FCSTD DOCUMENT  (FreeCAD 0.18R16146 (Git))
Label: mk-ltk-01_case-cover
License: All rights reserved
LicenseURL: http://en.wikipedia.org/wiki/All_rights_reserved
objects: Sketcher::SketchObject×12
note: 12 computed .brp shape members not serialized (recipe doc carries the construction recipe); baked Part::Feature solids carry a one-line shape summary decoded from their .brp

FEATURE [Sketcher::SketchObject] Sketch084  label="outer edge"
  MapMode = 2
  sketch-geometry (84):
    g0: LineSegment StartX=2.096 StartY=136.077 StartZ=0 EndX=419.671 EndY=136.077 EndZ=0
    g1: LineSegment StartX=421.665 StartY=134.233 StartZ=0 EndX=421.672 EndY=134.076 EndZ=0
    g2: LineSegment StartX=421.291 StartY=135.253 StartZ=0 EndX=421.375 EndY=135.122 EndZ=0
    g3: LineSegment StartX=421.647 StartY=134.39 StartZ=0 EndX=421.665 EndY=134.233 EndZ=0
    g4: LineSegment StartX=421.573 StartY=134.696 StartZ=0 EndX=421.615 EndY=134.543 EndZ=0
    g5: LineSegment StartX=420.846 StartY=0.63252 StartZ=0 EndX=420.716 EndY=0.545705 EndZ=0
    g6: LineSegment StartX=420.716 StartY=0.545705 StartZ=0 EndX=420.578 EndY=0.468535 EndZ=0
    g7: LineSegment StartX=420.578 StartY=0.468535 StartZ=0 EndX=420.437 EndY=0.403765 EndZ=0
    g8: LineSegment StartX=420.437 StartY=0.403765 StartZ=0 EndX=420.289 EndY=0.348644 EndZ=0
    g9: LineSegment StartX=420.97 StartY=135.598 StartZ=0 EndX=421.086 EndY=135.491 EndZ=0
    g10: LineSegment StartX=419.671 StartY=136.077 StartZ=0 EndX=419.827 EndY=136.07 EndZ=0
    g11: LineSegment StartX=421.192 StartY=135.376 StartZ=0 EndX=421.291 EndY=135.253 EndZ=0
    g12: LineSegment StartX=421.453 StartY=134.984 StartZ=0 EndX=421.52 EndY=134.842 EndZ=0
    g13: LineSegment StartX=421.453 StartY=1.34359 StartZ=0 EndX=421.375 EndY=1.20716 EndZ=0
    g14: LineSegment StartX=421.647 StartY=1.9389 StartZ=0 EndX=421.615 EndY=1.78456 EndZ=0
    g15: LineSegment StartX=421.615 StartY=1.78456 StartZ=0 EndX=421.573 EndY=1.63298 EndZ=0
    g16: LineSegment StartX=421.086 StartY=0.836468 StartZ=0 EndX=420.97 EndY=0.730359 EndZ=0
    g17: LineSegment StartX=420.97 StartY=0.730359 StartZ=0 EndX=420.846 EndY=0.63252 EndZ=0
    g18: LineSegment StartX=421.615 StartY=134.543 StartZ=0 EndX=421.647 EndY=134.39 EndZ=0
    g19: LineSegment StartX=421.573 StartY=1.63298 StartZ=0 EndX=421.52 EndY=1.48553 EndZ=0
    g20: LineSegment StartX=421.52 StartY=1.48553 StartZ=0 EndX=421.453 EndY=1.34359 EndZ=0
    g21: LineSegment StartX=421.672 StartY=2.25034 StartZ=0 EndX=421.665 EndY=2.09462 EndZ=0
    g22: LineSegment StartX=1.18787 StartY=0.468535 StartZ=0 EndX=1.05006 EndY=0.545705 EndZ=0
    g23: LineSegment StartX=1.05006 StartY=0.545705 StartZ=0 EndX=0.919152 EndY=0.63252 EndZ=0
    g24: LineSegment StartX=0.919152 StartY=0.63252 StartZ=0 EndX=0.796505 EndY=0.730359 EndZ=0
    g25: LineSegment StartX=0.796505 StartY=0.730359 StartZ=0 EndX=0.680752 EndY=0.836468 EndZ=0
    g26: LineSegment StartX=421.52 StartY=134.842 StartZ=0 EndX=421.573 EndY=134.696 EndZ=0
    g27: LineSegment StartX=0.101975 StartY=134.233 StartZ=0 EndX=0.119889 EndY=134.39 EndZ=0
    g28: LineSegment StartX=0.119889 StartY=134.39 StartZ=0 EndX=0.150206 EndY=134.543 EndZ=0
    g29: LineSegment StartX=0.150206 StartY=134.543 StartZ=0 EndX=0.192925 EndY=134.696 EndZ=0
    g30: LineSegment StartX=0.192925 StartY=134.696 StartZ=0 EndX=0.248047 EndY=134.842 EndZ=0
    g31: LineSegment StartX=421.665 StartY=2.09462 StartZ=0 EndX=421.647 EndY=1.9389 EndZ=0
    g32: LineSegment StartX=0.680752 StartY=0.836468 StartZ=0 EndX=0.574643 EndY=0.952225 EndZ=0
    g33: LineSegment StartX=0.574643 StartY=0.952225 StartZ=0 EndX=0.4768 EndY=1.07625 EndZ=0
    g34: LineSegment StartX=0.4768 StartY=1.07625 StartZ=0 EndX=0.389985 EndY=1.20716 EndZ=0
    g35: LineSegment StartX=0.389985 StartY=1.20716 StartZ=0 EndX=0.312815 EndY=1.34359 EndZ=0
    g36: LineSegment StartX=0.312815 StartY=1.34359 StartZ=0 EndX=0.248047 EndY=1.48553 EndZ=0
    g37: LineSegment StartX=0.248047 StartY=1.48553 StartZ=0 EndX=0.192925 EndY=1.63298 EndZ=0
    g38: LineSegment StartX=0.192925 StartY=1.63298 StartZ=0 EndX=0.150206 EndY=1.78456 EndZ=0
    g39: LineSegment StartX=0.150206 StartY=1.78456 StartZ=0 EndX=0.119889 EndY=1.9389 EndZ=0
    g40: LineSegment StartX=420.289 StartY=135.979 StartZ=0 EndX=420.437 EndY=135.924 EndZ=0
    g41: LineSegment StartX=1.7818 StartY=0.275608 StartZ=0 EndX=1.62884 EndY=0.307303 EndZ=0
    g42: LineSegment StartX=1.62884 StartY=0.307303 StartZ=0 EndX=1.47588 EndY=0.348644 EndZ=0
    g43: LineSegment StartX=1.47588 StartY=0.348644 StartZ=0 EndX=1.32981 EndY=0.403765 EndZ=0
    g44: LineSegment StartX=1.32981 StartY=0.403765 StartZ=0 EndX=1.18787 EndY=0.468535 EndZ=0
    g45: LineSegment StartX=420.437 StartY=135.924 StartZ=0 EndX=420.578 EndY=135.859 EndZ=0
    g46: LineSegment StartX=419.982 StartY=136.052 StartZ=0 EndX=420.137 EndY=136.022 EndZ=0
    g47: LineSegment StartX=419.827 StartY=136.07 StartZ=0 EndX=419.982 EndY=136.052 EndZ=0
    g48: LineSegment StartX=420.846 StartY=135.695 StartZ=0 EndX=420.97 EndY=135.598 EndZ=0
    g49: LineSegment StartX=420.578 StartY=135.859 StartZ=0 EndX=420.716 EndY=135.782 EndZ=0
    g50: LineSegment StartX=419.827 StartY=0.257693 StartZ=0 EndX=419.671 EndY=0.250803 EndZ=0
    g51: LineSegment StartX=419.671 StartY=0.250803 StartZ=0 EndX=2.096 EndY=0.250803 EndZ=0
    g52: LineSegment StartX=2.096 StartY=0.250803 StartZ=0 EndX=1.9389 EndY=0.257693 EndZ=0
    g53: LineSegment StartX=1.9389 StartY=0.257693 StartZ=0 EndX=1.7818 EndY=0.275608 EndZ=0
    g54: LineSegment StartX=0.248047 StartY=134.842 StartZ=0 EndX=0.312815 EndY=134.984 EndZ=0
    g55: LineSegment StartX=0.312815 StartY=134.984 StartZ=0 EndX=0.389985 EndY=135.122 EndZ=0
    g56: LineSegment StartX=0.389985 StartY=135.122 StartZ=0 EndX=0.4768 EndY=135.253 EndZ=0
    g57: LineSegment StartX=0.4768 StartY=135.253 StartZ=0 EndX=0.574643 EndY=135.376 EndZ=0
    g58: LineSegment StartX=0.574643 StartY=135.376 StartZ=0 EndX=0.680752 EndY=135.491 EndZ=0
    g59: LineSegment StartX=420.137 StartY=136.022 StartZ=0 EndX=420.289 EndY=135.979 EndZ=0
    g60: LineSegment StartX=420.716 StartY=135.782 StartZ=0 EndX=420.846 EndY=135.695 EndZ=0
    g61: LineSegment StartX=421.375 StartY=135.122 StartZ=0 EndX=421.453 EndY=134.984 EndZ=0
    g62: LineSegment StartX=420.289 StartY=0.348644 StartZ=0 EndX=420.137 EndY=0.307303 EndZ=0
    g63: LineSegment StartX=420.137 StartY=0.307303 StartZ=0 EndX=419.982 EndY=0.275608 EndZ=0
    g64: LineSegment StartX=419.982 StartY=0.275608 StartZ=0 EndX=419.827 EndY=0.257693 EndZ=0
    g65: LineSegment StartX=1.32981 StartY=135.924 StartZ=0 EndX=1.47588 EndY=135.979 EndZ=0
    g66: LineSegment StartX=1.47588 StartY=135.979 StartZ=0 EndX=1.62884 EndY=136.022 EndZ=0
    g67: LineSegment StartX=1.62884 StartY=136.022 StartZ=0 EndX=1.7818 EndY=136.052 EndZ=0
    g68: LineSegment StartX=1.7818 StartY=136.052 StartZ=0 EndX=1.9389 EndY=136.07 EndZ=0
    g69: LineSegment StartX=1.9389 StartY=136.07 StartZ=0 EndX=2.096 EndY=136.077 EndZ=0
    g70: LineSegment StartX=421.672 StartY=134.076 StartZ=0 EndX=421.672 EndY=2.25034 EndZ=0
    g71: LineSegment StartX=421.375 StartY=1.20716 StartZ=0 EndX=421.291 EndY=1.07625 EndZ=0
    g72: LineSegment StartX=421.291 StartY=1.07625 StartZ=0 EndX=421.192 EndY=0.952225 EndZ=0
    g73: LineSegment StartX=421.192 StartY=0.952225 StartZ=0 EndX=421.086 EndY=0.836468 EndZ=0
    g74: LineSegment StartX=421.086 StartY=135.491 StartZ=0 EndX=421.192 EndY=135.376 EndZ=0
    g75: LineSegment StartX=0.680752 StartY=135.491 StartZ=0 EndX=0.796505 EndY=135.598 EndZ=0
    g76: LineSegment StartX=0.796505 StartY=135.598 StartZ=0 EndX=0.919152 EndY=135.695 EndZ=0
    g77: LineSegment StartX=0.919152 StartY=135.695 StartZ=0 EndX=1.05006 EndY=135.782 EndZ=0
    g78: LineSegment StartX=1.05006 StartY=135.782 StartZ=0 EndX=1.18787 EndY=135.859 EndZ=0
    g79: LineSegment StartX=1.18787 StartY=135.859 StartZ=0 EndX=1.32981 EndY=135.924 EndZ=0
    g80: LineSegment StartX=0.119889 StartY=1.9389 StartZ=0 EndX=0.101975 EndY=2.09462 EndZ=0
    g81: LineSegment StartX=0.101975 StartY=2.09462 StartZ=0 EndX=0.0950846 EndY=2.25034 EndZ=0
    g82: LineSegment StartX=0.0950846 StartY=2.25034 StartZ=0 EndX=0.0950846 EndY=134.076 EndZ=0
    g83: LineSegment StartX=0.0950846 StartY=134.076 StartZ=0 EndX=0.101975 EndY=134.233 EndZ=0
FEATURE [Sketcher::SketchObject] Sketch092  label="arrow cluster"
  sketch-geometry (8):
    g0: LineSegment StartX=377.571 StartY=44.3523 StartZ=0 EndX=377.571 EndY=25.3022 EndZ=0
    g1: LineSegment StartX=377.571 StartY=25.3022 StartZ=0 EndX=358.521 EndY=25.3022 EndZ=0
    g2: LineSegment StartX=396.621 StartY=25.3022 StartZ=0 EndX=396.621 EndY=44.3523 EndZ=0
    g3: LineSegment StartX=396.621 StartY=44.3523 StartZ=0 EndX=377.571 EndY=44.3523 EndZ=0
    g4: LineSegment StartX=358.521 StartY=25.3022 StartZ=0 EndX=358.521 EndY=6.2508 EndZ=0
    g5: LineSegment StartX=358.521 StartY=6.2508 StartZ=0 EndX=415.671 EndY=6.2508 EndZ=0
    g6: LineSegment StartX=415.671 StartY=6.2508 StartZ=0 EndX=415.671 EndY=25.3022 EndZ=0
    g7: LineSegment StartX=415.671 StartY=25.3022 StartZ=0 EndX=396.621 EndY=25.3022 EndZ=0
FEATURE [Sketcher::SketchObject] Sketch098  label="main cluster"
  sketch-geometry (6):
    g0: LineSegment StartX=87.056 StartY=106.266 StartZ=0 EndX=87.056 EndY=11.0147 EndZ=0
    g1: LineSegment StartX=372.809 StartY=106.266 StartZ=0 EndX=87.056 EndY=106.266 EndZ=0
    g2: LineSegment StartX=372.809 StartY=30.0633 StartZ=0 EndX=372.809 EndY=106.266 EndZ=0
    g3: LineSegment StartX=348.995 StartY=11.0147 StartZ=0 EndX=348.995 EndY=30.0633 EndZ=0
    g4: LineSegment StartX=348.995 StartY=30.0633 StartZ=0 EndX=372.809 EndY=30.0633 EndZ=0
    g5: LineSegment StartX=87.056 StartY=11.0147 StartZ=0 EndX=348.995 EndY=11.0147 EndZ=0
FEATURE [Sketcher::SketchObject] Sketch130  label="num cluster"
  sketch-geometry (4):
    g0: LineSegment StartX=6.09367 StartY=106.266 StartZ=0 EndX=82.2964 EndY=106.266 EndZ=0
    g1: LineSegment StartX=82.2964 StartY=106.266 StartZ=0 EndX=82.2964 EndY=11.0147 EndZ=0
    g2: LineSegment StartX=82.2964 StartY=11.0147 StartZ=0 EndX=6.09367 EndY=11.0147 EndZ=0
    g3: LineSegment StartX=6.09367 StartY=11.0147 StartZ=0 EndX=6.09367 EndY=106.266 EndZ=0
FEATURE [Sketcher::SketchObject] Sketch  label="non macros cluster"
  sketch-geometry (4):
    g0: LineSegment StartX=377.571 StartY=106.266 StartZ=0 EndX=415.671 EndY=106.266 EndZ=0
    g1: LineSegment StartX=415.671 StartY=106.266 StartZ=0 EndX=415.671 EndY=49.1134 EndZ=0
    g2: LineSegment StartX=415.671 StartY=49.1134 StartZ=0 EndX=377.571 EndY=49.1134 EndZ=0
    g3: LineSegment StartX=377.571 StartY=49.1134 StartZ=0 EndX=377.571 EndY=106.266 EndZ=0
FEATURE [Sketcher::SketchObject] Sketch131  label="macros cluster"
  sketch-geometry (4):
    g0: LineSegment StartX=377.571 StartY=130.079 StartZ=0 EndX=415.671 EndY=130.079 EndZ=0
    g1: LineSegment StartX=415.671 StartY=130.079 StartZ=0 EndX=415.671 EndY=111.026 EndZ=0
    g2: LineSegment StartX=415.671 StartY=111.026 StartZ=0 EndX=377.571 EndY=111.026 EndZ=0
    g3: LineSegment StartX=377.571 StartY=111.026 StartZ=0 EndX=377.571 EndY=130.079 EndZ=0
FEATURE [Sketcher::SketchObject] Sketch132  label="print screen"
  sketch-geometry (4):
    g0: LineSegment StartX=353.755 StartY=130.079 StartZ=0 EndX=372.809 EndY=130.079 EndZ=0
    g1: LineSegment StartX=372.809 StartY=130.079 StartZ=0 EndX=372.809 EndY=111.026 EndZ=0
    g2: LineSegment StartX=372.809 StartY=111.026 StartZ=0 EndX=353.755 EndY=111.026 EndZ=0
    g3: LineSegment StartX=353.755 StartY=111.026 StartZ=0 EndX=353.755 EndY=130.079 EndZ=0
FEATURE [Sketcher::SketchObject] Sketch133  label="f912"
  sketch-geometry (4):
    g0: LineSegment StartX=272.795 StartY=130.079 StartZ=0 EndX=348.996 EndY=130.079 EndZ=0
    g1: LineSegment StartX=348.996 StartY=130.079 StartZ=0 EndX=348.996 EndY=111.026 EndZ=0
    g2: LineSegment StartX=348.996 StartY=111.026 StartZ=0 EndX=272.795 EndY=111.026 EndZ=0
    g3: LineSegment StartX=272.795 StartY=111.026 StartZ=0 EndX=272.795 EndY=130.079 EndZ=0
FEATURE [Sketcher::SketchObject] Sketch134  label="f58"
  sketch-geometry (4):
    g0: LineSegment StartX=191.831 StartY=130.079 StartZ=0 EndX=268.034 EndY=130.079 EndZ=0
    g1: LineSegment StartX=268.034 StartY=130.079 StartZ=0 EndX=268.034 EndY=111.026 EndZ=0
    g2: LineSegment StartX=268.034 StartY=111.026 StartZ=0 EndX=191.831 EndY=111.026 EndZ=0
    g3: LineSegment StartX=191.831 StartY=111.026 StartZ=0 EndX=191.831 EndY=130.079 EndZ=0
FEATURE [Sketcher::SketchObject] Sketch135  label="f14"
  sketch-geometry (4):
    g0: LineSegment StartX=110.87 StartY=130.079 StartZ=0 EndX=187.071 EndY=130.079 EndZ=0
    g1: LineSegment StartX=187.071 StartY=130.079 StartZ=0 EndX=187.071 EndY=111.026 EndZ=0
    g2: LineSegment StartX=187.071 StartY=111.026 StartZ=0 EndX=110.87 EndY=111.026 EndZ=0
    g3: LineSegment StartX=110.87 StartY=111.026 StartZ=0 EndX=110.87 EndY=130.079 EndZ=0
FEATURE [Sketcher::SketchObject] Sketch136  label="esc"
  sketch-geometry (4):
    g0: LineSegment StartX=87.056 StartY=130.079 StartZ=0 EndX=106.109 EndY=130.079 EndZ=0
    g1: LineSegment StartX=106.109 StartY=130.079 StartZ=0 EndX=106.109 EndY=111.026 EndZ=0
    g2: LineSegment StartX=106.109 StartY=111.026 StartZ=0 EndX=87.056 EndY=111.026 EndZ=0
    g3: LineSegment StartX=87.056 StartY=111.026 StartZ=0 EndX=87.056 EndY=130.079 EndZ=0
FEATURE [Sketcher::SketchObject] Sketch137
  sketch-geometry (130):
    g0: LineSegment StartX=2.096 StartY=136.077 StartZ=0 EndX=419.671 EndY=136.077 EndZ=0
    g1: LineSegment StartX=421.665 StartY=134.233 StartZ=0 EndX=421.672 EndY=134.076 EndZ=0
    g2: LineSegment StartX=421.291 StartY=135.253 StartZ=0 EndX=421.375 EndY=135.122 EndZ=0
    g3: LineSegment StartX=421.647 StartY=134.39 StartZ=0 EndX=421.665 EndY=134.233 EndZ=0
    g4: LineSegment StartX=421.573 StartY=134.696 StartZ=0 EndX=421.615 EndY=134.543 EndZ=0
    g5: LineSegment StartX=420.846 StartY=0.63252 StartZ=0 EndX=420.716 EndY=0.545705 EndZ=0
    g6: LineSegment StartX=420.716 StartY=0.545705 StartZ=0 EndX=420.578 EndY=0.468535 EndZ=0
    g7: LineSegment StartX=420.578 StartY=0.468535 StartZ=0 EndX=420.437 EndY=0.403765 EndZ=0
    g8: LineSegment StartX=420.437 StartY=0.403765 StartZ=0 EndX=420.289 EndY=0.348644 EndZ=0
    g9: LineSegment StartX=420.97 StartY=135.598 StartZ=0 EndX=421.086 EndY=135.491 EndZ=0
    g10: LineSegment StartX=419.671 StartY=136.077 StartZ=0 EndX=419.827 EndY=136.07 EndZ=0
    g11: LineSegment StartX=421.192 StartY=135.376 StartZ=0 EndX=421.291 EndY=135.253 EndZ=0
    g12: LineSegment StartX=421.453 StartY=134.984 StartZ=0 EndX=421.52 EndY=134.842 EndZ=0
    g13: LineSegment StartX=421.453 StartY=1.34359 StartZ=0 EndX=421.375 EndY=1.20716 EndZ=0
    g14: LineSegment StartX=421.647 StartY=1.9389 StartZ=0 EndX=421.615 EndY=1.78456 EndZ=0
    g15: LineSegment StartX=421.615 StartY=1.78456 StartZ=0 EndX=421.573 EndY=1.63298 EndZ=0
    g16: LineSegment StartX=421.086 StartY=0.836468 StartZ=0 EndX=420.97 EndY=0.730359 EndZ=0
    g17: LineSegment StartX=420.97 StartY=0.730359 StartZ=0 EndX=420.846 EndY=0.63252 EndZ=0
    g18: LineSegment StartX=421.615 StartY=134.543 StartZ=0 EndX=421.647 EndY=134.39 EndZ=0
    g19: LineSegment StartX=421.573 StartY=1.63298 StartZ=0 EndX=421.52 EndY=1.48553 EndZ=0
    g20: LineSegment StartX=421.52 StartY=1.48553 StartZ=0 EndX=421.453 EndY=1.34359 EndZ=0
    g21: LineSegment StartX=421.672 StartY=2.25034 StartZ=0 EndX=421.665 EndY=2.09462 EndZ=0
    g22: LineSegment StartX=1.18787 StartY=0.468535 StartZ=0 EndX=1.05006 EndY=0.545705 EndZ=0
    g23: LineSegment StartX=1.05006 StartY=0.545705 StartZ=0 EndX=0.919152 EndY=0.63252 EndZ=0
    g24: LineSegment StartX=0.919152 StartY=0.63252 StartZ=0 EndX=0.796505 EndY=0.730359 EndZ=0
    g25: LineSegment StartX=0.796505 StartY=0.730359 StartZ=0 EndX=0.680752 EndY=0.836468 EndZ=0
    g26: LineSegment StartX=421.52 StartY=134.842 StartZ=0 EndX=421.573 EndY=134.696 EndZ=0
    g27: LineSegment StartX=0.101975 StartY=134.233 StartZ=0 EndX=0.119889 EndY=134.39 EndZ=0
    g28: LineSegment StartX=0.119889 StartY=134.39 StartZ=0 EndX=0.150206 EndY=134.543 EndZ=0
    g29: LineSegment StartX=0.150206 StartY=134.543 StartZ=0 EndX=0.192925 EndY=134.696 EndZ=0
    g30: LineSegment StartX=0.192925 StartY=134.696 StartZ=0 EndX=0.248047 EndY=134.842 EndZ=0
    g31: LineSegment StartX=421.665 StartY=2.09462 StartZ=0 EndX=421.647 EndY=1.9389 EndZ=0
    g32: LineSegment StartX=0.680752 StartY=0.836468 StartZ=0 EndX=0.574643 EndY=0.952225 EndZ=0
    g33: LineSegment StartX=0.574643 StartY=0.952225 StartZ=0 EndX=0.4768 EndY=1.07625 EndZ=0
    g34: LineSegment StartX=0.4768 StartY=1.07625 StartZ=0 EndX=0.389985 EndY=1.20716 EndZ=0
    g35: LineSegment StartX=0.389985 StartY=1.20716 StartZ=0 EndX=0.312815 EndY=1.34359 EndZ=0
    g36: LineSegment StartX=0.312815 StartY=1.34359 StartZ=0 EndX=0.248047 EndY=1.48553 EndZ=0
    g37: LineSegment StartX=0.248047 StartY=1.48553 StartZ=0 EndX=0.192925 EndY=1.63298 EndZ=0
    g38: LineSegment StartX=0.192925 StartY=1.63298 StartZ=0 EndX=0.150206 EndY=1.78456 EndZ=0
    g39: LineSegment StartX=0.150206 StartY=1.78456 StartZ=0 EndX=0.119889 EndY=1.9389 EndZ=0
    g40: LineSegment StartX=420.289 StartY=135.979 StartZ=0 EndX=420.437 EndY=135.924 EndZ=0
    g41: LineSegment StartX=1.7818 StartY=0.275608 StartZ=0 EndX=1.62884 EndY=0.307303 EndZ=0
    g42: LineSegment StartX=1.62884 StartY=0.307303 StartZ=0 EndX=1.47588 EndY=0.348644 EndZ=0
    g43: LineSegment StartX=1.47588 StartY=0.348644 StartZ=0 EndX=1.32981 EndY=0.403765 EndZ=0
    g44: LineSegment StartX=1.32981 StartY=0.403765 StartZ=0 EndX=1.18787 EndY=0.468535 EndZ=0
    g45: LineSegment StartX=420.437 StartY=135.924 StartZ=0 EndX=420.578 EndY=135.859 EndZ=0
    g46: LineSegment StartX=419.982 StartY=136.052 StartZ=0 EndX=420.137 EndY=136.022 EndZ=0
    g47: LineSegment StartX=419.827 StartY=136.07 StartZ=0 EndX=419.982 EndY=136.052 EndZ=0
    g48: LineSegment StartX=420.846 StartY=135.695 StartZ=0 EndX=420.97 EndY=135.598 EndZ=0
    g49: LineSegment StartX=420.578 StartY=135.859 StartZ=0 EndX=420.716 EndY=135.782 EndZ=0
    g50: LineSegment StartX=419.827 StartY=0.257693 StartZ=0 EndX=419.671 EndY=0.250803 EndZ=0
    g51: LineSegment StartX=419.671 StartY=0.250803 StartZ=0 EndX=2.096 EndY=0.250803 EndZ=0
    g52: LineSegment StartX=2.096 StartY=0.250803 StartZ=0 EndX=1.9389 EndY=0.257693 EndZ=0
    g53: LineSegment StartX=1.9389 StartY=0.257693 StartZ=0 EndX=1.7818 EndY=0.275608 EndZ=0
    g54: LineSegment StartX=0.248047 StartY=134.842 StartZ=0 EndX=0.312815 EndY=134.984 EndZ=0
    g55: LineSegment StartX=0.312815 StartY=134.984 StartZ=0 EndX=0.389985 EndY=135.122 EndZ=0
    g56: LineSegment StartX=0.389985 StartY=135.122 StartZ=0 EndX=0.4768 EndY=135.253 EndZ=0
    g57: LineSegment StartX=0.4768 StartY=135.253 StartZ=0 EndX=0.574643 EndY=135.376 EndZ=0
    g58: LineSegment StartX=0.574643 StartY=135.376 StartZ=0 EndX=0.680752 EndY=135.491 EndZ=0
    g59: LineSegment StartX=420.137 StartY=136.022 StartZ=0 EndX=420.289 EndY=135.979 EndZ=0
    g60: LineSegment StartX=420.716 StartY=135.782 StartZ=0 EndX=420.846 EndY=135.695 EndZ=0
    g61: LineSegment StartX=421.375 StartY=135.122 StartZ=0 EndX=421.453 EndY=134.984 EndZ=0
    g62: LineSegment StartX=420.289 StartY=0.348644 StartZ=0 EndX=420.137 EndY=0.307303 EndZ=0
    g63: LineSegment StartX=420.137 StartY=0.307303 StartZ=0 EndX=419.982 EndY=0.275608 EndZ=0
    g64: LineSegment StartX=419.982 StartY=0.275608 StartZ=0 EndX=419.827 EndY=0.257693 EndZ=0
    g65: LineSegment StartX=1.32981 StartY=135.924 StartZ=0 EndX=1.47588 EndY=135.979 EndZ=0
    g66: LineSegment StartX=1.47588 StartY=135.979 StartZ=0 EndX=1.62884 EndY=136.022 EndZ=0
    g67: LineSegment StartX=1.62884 StartY=136.022 StartZ=0 EndX=1.7818 EndY=136.052 EndZ=0
    g68: LineSegment StartX=1.7818 StartY=136.052 StartZ=0 EndX=1.9389 EndY=136.07 EndZ=0
    g69: LineSegment StartX=1.9389 StartY=136.07 StartZ=0 EndX=2.096 EndY=136.077 EndZ=0
    g70: LineSegment StartX=421.672 StartY=134.076 StartZ=0 EndX=421.672 EndY=2.25034 EndZ=0
    g71: LineSegment StartX=421.375 StartY=1.20716 StartZ=0 EndX=421.291 EndY=1.07625 EndZ=0
    g72: LineSegment StartX=421.291 StartY=1.07625 StartZ=0 EndX=421.192 EndY=0.952225 EndZ=0
    g73: LineSegment StartX=421.192 StartY=0.952225 StartZ=0 EndX=421.086 EndY=0.836468 EndZ=0
    g74: LineSegment StartX=421.086 StartY=135.491 StartZ=0 EndX=421.192 EndY=135.376 EndZ=0
    g75: LineSegment StartX=0.680752 StartY=135.491 StartZ=0 EndX=0.796505 EndY=135.598 EndZ=0
    g76: LineSegment StartX=0.796505 StartY=135.598 StartZ=0 EndX=0.919152 EndY=135.695 EndZ=0
    g77: LineSegment StartX=0.919152 StartY=135.695 StartZ=0 EndX=1.05006 EndY=135.782 EndZ=0
    g78: LineSegment StartX=1.05006 StartY=135.782 StartZ=0 EndX=1.18787 EndY=135.859 EndZ=0
    g79: LineSegment StartX=1.18787 StartY=135.859 StartZ=0 EndX=1.32981 EndY=135.924 EndZ=0
    g80: LineSegment StartX=0.119889 StartY=1.9389 StartZ=0 EndX=0.101975 EndY=2.09462 EndZ=0
    g81: LineSegment StartX=0.101975 StartY=2.09462 StartZ=0 EndX=0.0950846 EndY=2.25034 EndZ=0
    g82: LineSegment StartX=0.0950846 StartY=2.25034 StartZ=0 EndX=0.0950846 EndY=134.076 EndZ=0
    g83: LineSegment StartX=0.0950846 StartY=134.076 StartZ=0 EndX=0.101975 EndY=134.233 EndZ=0
    g84: LineSegment StartX=110.87 StartY=130.079 StartZ=0 EndX=187.071 EndY=130.079 EndZ=0
    g85: LineSegment StartX=187.071 StartY=130.079 StartZ=0 EndX=187.071 EndY=111.026 EndZ=0
    g86: LineSegment StartX=187.071 StartY=111.026 StartZ=0 EndX=110.87 EndY=111.026 EndZ=0
    g87: LineSegment StartX=110.87 StartY=111.026 StartZ=0 EndX=110.87 EndY=130.079 EndZ=0
    g88: LineSegment StartX=6.09367 StartY=106.266 StartZ=0 EndX=82.2964 EndY=106.266 EndZ=0
    g89: LineSegment StartX=82.2964 StartY=106.266 StartZ=0 EndX=82.2964 EndY=11.0147 EndZ=0
    g90: LineSegment StartX=82.2964 StartY=11.0147 StartZ=0 EndX=6.09367 EndY=11.0147 EndZ=0
    g91: LineSegment StartX=6.09367 StartY=11.0147 StartZ=0 EndX=6.09367 EndY=106.266 EndZ=0
    g92: LineSegment StartX=191.831 StartY=130.079 StartZ=0 EndX=268.034 EndY=130.079 EndZ=0
    g93: LineSegment StartX=268.034 StartY=130.079 StartZ=0 EndX=268.034 EndY=111.026 EndZ=0
    g94: LineSegment StartX=268.034 StartY=111.026 StartZ=0 EndX=191.831 EndY=111.026 EndZ=0
    g95: LineSegment StartX=191.831 StartY=111.026 StartZ=0 EndX=191.831 EndY=130.079 EndZ=0
    g96: LineSegment StartX=272.795 StartY=130.079 StartZ=0 EndX=348.996 EndY=130.079 EndZ=0
    g97: LineSegment StartX=348.996 StartY=130.079 StartZ=0 EndX=348.996 EndY=111.026 EndZ=0
    g98: LineSegment StartX=348.996 StartY=111.026 StartZ=0 EndX=272.795 EndY=111.026 EndZ=0
    g99: LineSegment StartX=272.795 StartY=111.026 StartZ=0 EndX=272.795 EndY=130.079 EndZ=0
    g100: LineSegment StartX=377.571 StartY=130.079 StartZ=0 EndX=415.671 EndY=130.079 EndZ=0
    g101: LineSegment StartX=415.671 StartY=130.079 StartZ=0 EndX=415.671 EndY=111.026 EndZ=0
    g102: LineSegment StartX=415.671 StartY=111.026 StartZ=0 EndX=377.571 EndY=111.026 EndZ=0
    g103: LineSegment StartX=377.571 StartY=111.026 StartZ=0 EndX=377.571 EndY=130.079 EndZ=0
    g104: LineSegment StartX=353.755 StartY=130.079 StartZ=0 EndX=372.809 EndY=130.079 EndZ=0
    g105: LineSegment StartX=372.809 StartY=130.079 StartZ=0 EndX=372.809 EndY=111.026 EndZ=0
    g106: LineSegment StartX=372.809 StartY=111.026 StartZ=0 EndX=353.755 EndY=111.026 EndZ=0
    g107: LineSegment StartX=353.755 StartY=111.026 StartZ=0 EndX=353.755 EndY=130.079 EndZ=0
    g108: LineSegment StartX=377.571 StartY=106.266 StartZ=0 EndX=415.671 EndY=106.266 EndZ=0
    g109: LineSegment StartX=415.671 StartY=106.266 StartZ=0 EndX=415.671 EndY=49.1134 EndZ=0
    g110: LineSegment StartX=415.671 StartY=49.1134 StartZ=0 EndX=377.571 EndY=49.1134 EndZ=0
    g111: LineSegment StartX=377.571 StartY=49.1134 StartZ=0 EndX=377.571 EndY=106.266 EndZ=0
    g112: LineSegment StartX=87.056 StartY=130.079 StartZ=0 EndX=106.109 EndY=130.079 EndZ=0
    g113: LineSegment StartX=106.109 StartY=130.079 StartZ=0 EndX=106.109 EndY=111.026 EndZ=0
    g114: LineSegment StartX=106.109 StartY=111.026 StartZ=0 EndX=87.056 EndY=111.026 EndZ=0
    g115: LineSegment StartX=87.056 StartY=111.026 StartZ=0 EndX=87.056 EndY=130.079 EndZ=0
    g116: LineSegment StartX=377.571 StartY=44.3523 StartZ=0 EndX=377.571 EndY=25.3022 EndZ=0
    g117: LineSegment StartX=377.571 StartY=25.3022 StartZ=0 EndX=358.521 EndY=25.3022 EndZ=0
    g118: LineSegment StartX=396.621 StartY=25.3022 StartZ=0 EndX=396.621 EndY=44.3523 EndZ=0
    g119: LineSegment StartX=396.621 StartY=44.3523 StartZ=0 EndX=377.571 EndY=44.3523 EndZ=0
    g120: LineSegment StartX=358.521 StartY=25.3022 StartZ=0 EndX=358.521 EndY=6.2508 EndZ=0
    g121: LineSegment StartX=358.521 StartY=6.2508 StartZ=0 EndX=415.671 EndY=6.2508 EndZ=0
    g122: LineSegment StartX=415.671 StartY=6.2508 StartZ=0 EndX=415.671 EndY=25.3022 EndZ=0
    g123: LineSegment StartX=415.671 StartY=25.3022 StartZ=0 EndX=396.621 EndY=25.3022 EndZ=0
    g124: LineSegment StartX=87.056 StartY=106.266 StartZ=0 EndX=87.056 EndY=11.0147 EndZ=0
    g125: LineSegment StartX=372.809 StartY=106.266 StartZ=0 EndX=87.056 EndY=106.266 EndZ=0
    g126: LineSegment StartX=372.809 StartY=30.0633 StartZ=0 EndX=372.809 EndY=106.266 EndZ=0
    g127: LineSegment StartX=348.995 StartY=11.0147 StartZ=0 EndX=348.995 EndY=30.0633 EndZ=0
    g128: LineSegment StartX=348.995 StartY=30.0633 StartZ=0 EndX=372.809 EndY=30.0633 EndZ=0
    g129: LineSegment StartX=87.056 StartY=11.0147 StartZ=0 EndX=348.995 EndY=11.0147 EndZ=0
